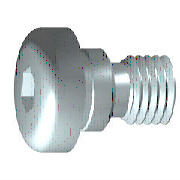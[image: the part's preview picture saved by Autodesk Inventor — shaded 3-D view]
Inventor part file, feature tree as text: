
AUTODESK INVENTOR PART (.ipt)
format: ipt  version: 2019.4 (Build 234330000, 330)  size: 226,304 bytes
history: native  units: mm (DEFAULTED — no unit token found)
features: sketch x2, other x2, extrude x1
ambient origin geometry x7: Origin, YZ Plane, XZ Plane, X Axis, Y Axis, Z Axis, Center Point
bodies: Solid1 (feature_tree), Body (feature_tree)
feature tree (5):
  sketch  "Sketch1"  dims[d0=4.826mm d1=6.2992mm]
  extrude  "Slot"  Depth=6.2992mm
  other  "Groove1"
  other  "Groove2"
  sketch  "Sketch2"  dims[d2=9.525mm d3=3.666174mm d5=9.525mm d6=4.7752mm d7=2.3876mm d8=60.0deg d9=17.4625mm d10=90.0deg d11=10.0mm d12=0.0mm d13=2.3622mm d14=0.62992mm d15=0.62992mm d16=0.127mm d17=45.0deg d19=45.0deg d20=5.7658mm d21=3.56616mm d22=45.0deg d23=2.1082mm d25=9.525mm d26=0.0mm d27=90.0deg d29=0.0mm d30=90.0deg d31=45.0deg d32=0.7366mm d33=0.0mm d34=2.3622mm d35=0.0mm]
